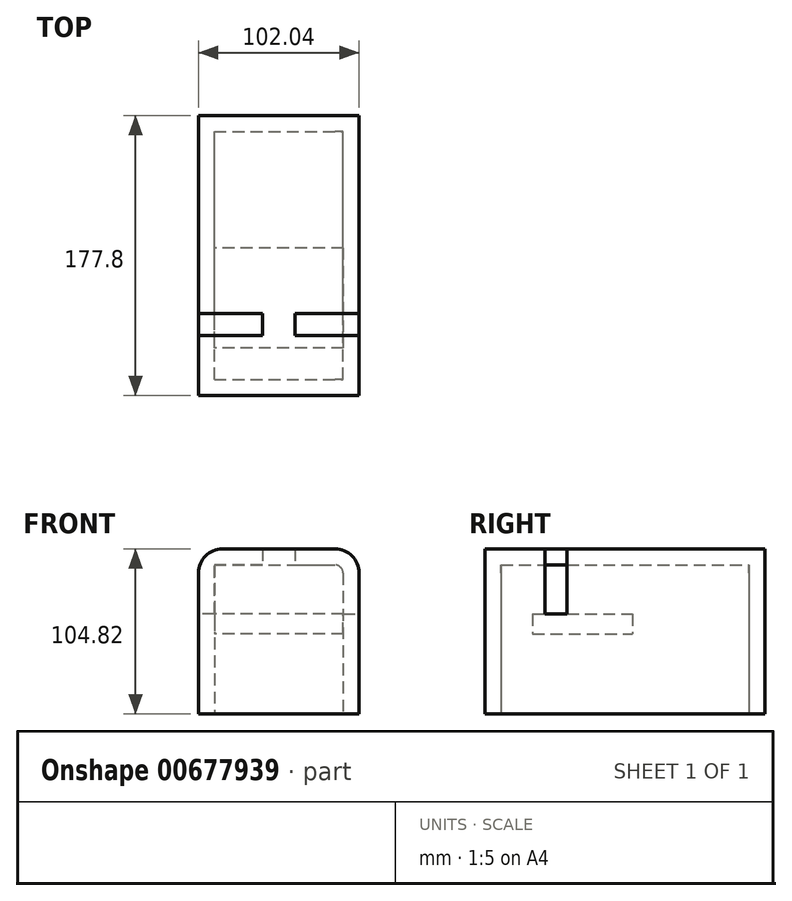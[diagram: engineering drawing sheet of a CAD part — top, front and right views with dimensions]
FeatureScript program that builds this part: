
annotation { "Feature Type Name" : "Feature", "Feature Type Description" : "" }
export const myFeature = defineFeature(function(context is Context, id is Id, definition is map)
    precondition{}
    {
        {
            var Q0;
            Q0=qCreatedBy(makeId("Front.planeOp"),FACE);
            var sketch = newSketch(context, id + "F0", { "sketchPlane" : qUnion([Q0])});
            skLineSegment(sketch, "E0.bottom", {"start": v(-47.42, 49.33) * mm, "end": v(54.62, 49.33) * mm});
            skLineSegment(sketch, "E0.top", {"start": v(-47.42, -55.5) * mm, "end": v(54.62, -55.5) * mm});
            skLineSegment(sketch, "E0.left", {"start": v(-47.42, 49.33) * mm, "end": v(-47.42, -55.5) * mm});
            skLineSegment(sketch, "E0.right", {"start": v(54.62, 49.33) * mm, "end": v(54.62, -55.5) * mm});
            skSolve(sketch);
        }
        {
            var Q0;
            Q0 = qSketchRegion(id + "F0", true);
            extrude(context, id + "F1", {"entities" : qUnion([Q0]), "depth" : 177.8 * mm, "offsetDistance" : 25.4 * mm});
        }
        {
            var Q0;
            Q0=makeQuery(id+"F1.opExtrude","SWEPT_EDGE",EDGE,{"disambiguationData":[OSD([sQuery(id+"F0.wireOp",EDGE,"E0.bottom"),sQuery(id+"F0.wireOp",EDGE,"E0.right")])]});
            fillet(context, id + "F2", {"entities" : qUnion([Q0]), "radius" : 15.24 * mm, "tangentPropagation" : true, "allowEdgeOverflow" : false});
        }
        {
            var Q0;
            Q0=makeQuery(id+"F1.opExtrude","SWEPT_FACE",FACE,{"disambiguationData":[OSD([sQuery(id+"F0.wireOp",EDGE,"E0.top")])]});
            shell(context, id + "F3", {"entities" : qUnion([Q0]), "thickness" : 10.16 * mm});
        }
        {
            var Q0;
            Q0=makeQuery(id+"F1.opExtrude","SWEPT_FACE",FACE,{"disambiguationData":[OSD([sQuery(id+"F0.wireOp",EDGE,"E0.right")])]});
            var sketch = newSketch(context, id + "F4", { "sketchPlane" : qUnion([Q0])});
            skLineSegment(sketch, "E1.bottom", {"start": v(-139.7, 55.34) * mm, "end": v(-125.73, 55.34) * mm});
            skLineSegment(sketch, "E1.top", {"start": v(-139.7, 8) * mm, "end": v(-125.73, 8) * mm});
            skLineSegment(sketch, "E1.left", {"start": v(-139.7, 55.34) * mm, "end": v(-139.7, 8) * mm});
            skLineSegment(sketch, "E1.right", {"start": v(-125.73, 55.34) * mm, "end": v(-125.73, 8) * mm});
            skSolve(sketch);
        }
        {
            var Q0;
            Q0=makeQuery(id+"F1.opExtrude","SWEPT_FACE",FACE,{"disambiguationData":[OSD([sQuery(id+"F0.wireOp",EDGE,"E0.left")])]});
            var sketch = newSketch(context, id + "F5", { "sketchPlane" : qUnion([Q0])});
            skLineSegment(sketch, "E2.bottom", {"start": v(125.73, 54.5) * mm, "end": v(139.7, 54.5) * mm});
            skLineSegment(sketch, "E2.top", {"start": v(125.73, 8) * mm, "end": v(139.7, 8) * mm});
            skLineSegment(sketch, "E2.left", {"start": v(125.73, 54.5) * mm, "end": v(125.73, 8) * mm});
            skLineSegment(sketch, "E2.right", {"start": v(139.7, 54.5) * mm, "end": v(139.7, 8) * mm});
            skSolve(sketch);
        }
        {
            var Q0;
            {var subQ0=sQuery(id+"F4.wireOp",EDGE,"E1.bottom");Q0=makeQuery(id+"F4.imprint","IMPRINT",FACE,{"disambiguationData":[TD([[makeQuery(id+"F4.imprint","IMPRINT",EDGE,{"derivedFrom":subQ0}),-1.0]])]});}
            var Q1;
            {var subQ0=sQuery(id+"F4.wireOp",EDGE,"E1.top");Q1=makeQuery(id+"F4.imprint","IMPRINT",FACE,{"disambiguationData":[TD([[makeQuery(id+"F4.imprint","IMPRINT",EDGE,{"derivedFrom":subQ0}),1.0]])]});}
            extrude(context, id + "F6", {"entities" : qUnion([Q0, Q1]), "operationType" : NewBodyOperationType.REMOVE, "oppositeDirection" : true, "depth" : 40.64 * mm, "offsetDistance" : 25.4 * mm});
        }
        {
            var Q0;
            Q0 = qSketchRegion(id + "F5", true);
            extrude(context, id + "F7", {"entities" : qUnion([Q0]), "operationType" : NewBodyOperationType.REMOVE, "oppositeDirection" : true, "depth" : 40.64 * mm, "offsetDistance" : 25.4 * mm});
        }
        {
            var Q0;
            Q0=makeQuery(id+"F1.opExtrude","SWEPT_EDGE",EDGE,{"disambiguationData":[OSD([sQuery(id+"F0.wireOp",EDGE,"E0.bottom"),sQuery(id+"F0.wireOp",EDGE,"E0.left")])]});
            fillet(context, id + "F8", {"entities" : qUnion([Q0]), "radius" : 15.24 * mm, "tangentPropagation" : true, "allowEdgeOverflow" : false});
        }
        {
            var Q0;
            Q0=makeQuery(id+"F3.opShell","OFFSET_FACE",FACE,{"disambiguationData":[OSD([sQuery(id+"F0.wireOp",EDGE,"E0.left")])]});
            var sketch = newSketch(context, id + "F9", { "sketchPlane" : qUnion([Q0])});
            skSolve(sketch);
        }
        {
            var Q0;
            {var subQ0=sQuery(id+"F0.wireOp",EDGE,"E0.left");Q0=makeQuery(id+"F9.imprint","IMPRINT",FACE,{"disambiguationData":[TD([[makeQuery(id+"F9.imprint","IMPRINT",EDGE,{"derivedFrom":makeQuery(id+"F3.opShell","OFFSET_EDGE",EDGE,{"disambiguationData":[OSD([subQ0]),TDD([makeQuery(id+"F1.opExtrude","CAP_EDGE",EDGE,{"disambiguationData":[OSD([subQ0])],"isStart":true})])]})}),-1.0]])]});}
            var sketch = newSketch(context, id + "F10", { "sketchPlane" : qUnion([Q0])});
            skLineSegment(sketch, "E3.bottom", {"start": v(-147.6, 8) * mm, "end": v(-84.1, 8) * mm});
            skLineSegment(sketch, "E3.top", {"start": v(-147.6, -4.7) * mm, "end": v(-84.1, -4.7) * mm});
            skLineSegment(sketch, "E3.left", {"start": v(-147.6, 8) * mm, "end": v(-147.6, -4.7) * mm});
            skLineSegment(sketch, "E3.right", {"start": v(-84.1, 8) * mm, "end": v(-84.1, -4.7) * mm});
            skSolve(sketch);
        }
        {
            var Q0;
            Q0 = qSketchRegion(id + "F10", true);
            extrude(context, id + "F11", {"entities" : qUnion([Q0]), "operationType" : NewBodyOperationType.ADD, "depth" : 91.19 * mm, "offsetDistance" : 25.4 * mm});
        }
    });
